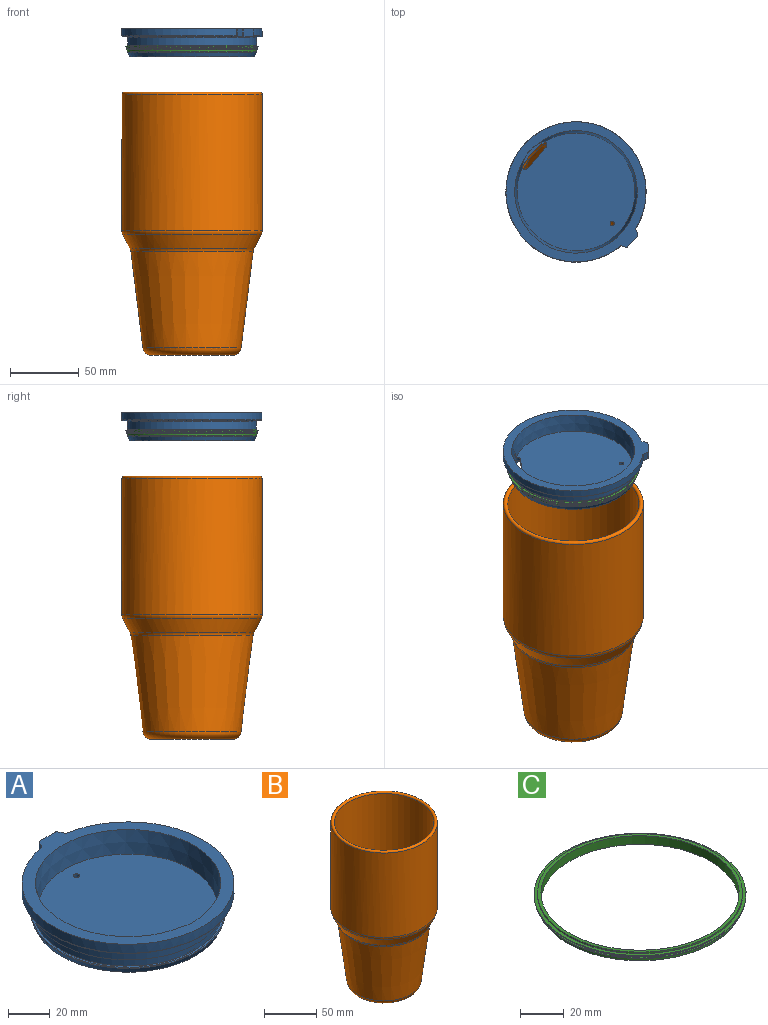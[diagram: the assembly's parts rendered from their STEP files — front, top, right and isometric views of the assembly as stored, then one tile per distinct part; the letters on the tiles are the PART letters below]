
ASSEMBLY  parts=3 mates=5
PART A: 35 faces, bbox 110x110x20.3 mm
  f0: cone r=44.45mm half-angle=7.6deg, axis (0,0,1), area 3346.1mm2, adj f1,f3,f19,f20,f21
  f1: plane 85.41x83.51mm, normal (0,0,1), area 5610.9mm2, adj f0,f16,f17,f18,f19,f20,f23
  f2: plane 85.41x83.51mm, normal (0,0,-1), area 5610.9mm2, adj f15,f16,f17,f18,f19,f20,f23
  f3: plane 105.36x101.6mm, normal (0,0,1), area 1950.2mm2, adj f0,f4,f21,f27,f28,f29,f30,f31
  f4: cylinder r=50.8mm len=101.6mm, axis (0,0,-1), area 1583.8mm2, adj f3,f5,f27,f33
  f5: torus R=50.39mm, axis (0,0,-1), area 200mm2, adj f4,f6,f24,f25,f26,f27,f33
  f6: plane 100.79x100.79mm, normal (0,0,-1), area 870.9mm2, adj f5,f7
  f7: torus R=47.56mm, axis (0,0,-1), area 365.7mm2, adj f6,f8
  f8: cylinder r=46.78mm len=93.55mm, axis (0,0,-1), area 1634.9mm2, adj f7,f9
  f9: plane 93.55x93.55mm, normal (0,0,-1), area 458.7mm2, adj f8,f10
  f10: cylinder r=45.19mm len=90.38mm, axis (0,0,-1), area 1352.2mm2, adj f9,f11
  f11: plane 92.6x92.6mm, normal (0,0,1), area 318.7mm2, adj f10,f12
  f12: torus R=46.3mm, axis (0,0,-1), area 180.7mm2, adj f11,f13
  f13: cone r=46.58mm half-angle=24deg, axis (0,0,1), area 986.6mm2, adj f12,f14
  f14: plane 90.38x90.38mm, normal (0,0,-1), area 686.4mm2, adj f13,f15
  f15: cylinder r=42.7mm len=85.41mm, axis (0,0,-1), area 1241.1mm2, adj f2,f14,f19,f20,f22
  f16: plane 20.19x2.54mm, normal (0,-1,0), area 51.3mm2, adj f1,f2,f17,f18
  f17: cylinder r=3.17mm len=3.14mm, axis (0,0,1), area 11.3mm2, adj f1,f2,f16,f19
  f18: cylinder r=3.17mm len=2.54mm, axis (0,0,1), area 8mm2, adj f1,f2,f16,f20
  f19: cylinder r=1.3mm len=7.04mm, axis (0,0,1), area 6.5mm2, adj f0,f1,f2,f15,f17,f21,f22
  f20: cylinder r=1.3mm len=4.64mm, axis (0,0,1), area 5mm2, adj f0,f1,f2,f15,f18,f21,f22
  f21: cylinder r=22.36mm len=24.5mm, axis (0,0,1), area 357.6mm2, adj f0,f3,f19,f20,f22
  f22: plane 25.42x4.26mm, normal (0,0,1), area 41.9mm2, adj f15,f19,f20,f21
  f23: cylinder r=1.52mm len=3.05mm, axis (0,0,1), area 24.3mm2, adj f1,f2
  f24: plane 0.43x0.22mm, normal (0.16,-0.99,0), area 0.1mm2, adj f5,f25,f33,f34
  f25: cylinder r=50.15mm len=16.4mm, axis (0,0,1), area 3.6mm2, adj f5,f24,f26,f34
  f26: plane 0.43x0.22mm, normal (-0.16,-0.99,0), area 0.1mm2, adj f5,f25,f27,f34
  f27: cylinder r=0.85mm len=5.64mm, axis (0,0,1), area 3.1mm2, adj f3,f4,f5,f26,f28,f34
  f28: plane 5.64x3.39mm, normal (0.89,0.45,0), area 21.4mm2, adj f3,f27,f29,f34
  f29: cylinder r=1.27mm len=5.64mm, axis (0,0,1), area 7.9mm2, adj f3,f28,f30,f34
  f30: plane 10.3x5.64mm, normal (0,1,0), area 58.1mm2, adj f3,f29,f31,f34
  f31: cylinder r=1.27mm len=5.64mm, axis (0,0,1), area 7.9mm2, adj f3,f30,f32,f34
  f32: plane 5.64x3.39mm, normal (-0.89,0.45,0), area 21.4mm2, adj f3,f31,f33,f34
  f33: cylinder r=0.85mm len=5.64mm, axis (0,0,1), area 3.1mm2, adj f3,f4,f5,f24,f32,f34
  f34: plane 17.25x4.54mm, normal (0,0,-1), area 55.7mm2, adj f24,f25,f26,f27,f28,f29,f30,f31
PART B: 14 faces, bbox 110x110x190.6 mm
  f0: plane 55.28x55.28mm, normal (0,0,1), area 2399.7mm2, adj f13
  f1: cone r=41.3mm half-angle=7.1deg, axis (0,0,1), area 16153.7mm2, adj f2,f13
  f2: torus R=44.45mm, axis (0,0,1), area 280.4mm2, adj f1,f3
  f3: cone r=47.62mm half-angle=26.6deg, axis (0,0,1), area 3770.4mm2, adj f2,f4
  f4: cylinder r=47.62mm len=99.37mm, axis (0,0,1), area 29734.9mm2, adj f3,f5
  f5: torus R=49.21mm, axis (0,0,1), area 1542.1mm2, adj f4,f6
  f6: cylinder r=50.8mm len=101.6mm, axis (0,0,1), area 31478mm2, adj f5,f10
  f7: cone r=50.8mm half-angle=26.6deg, axis (0,0,1), area 3468.1mm2, adj f10,f11
  f8: cone r=44.45mm half-angle=7.1deg, axis (0,0,1), area 17603.7mm2, adj f11,f12
  f9: plane 58.64x58.64mm, normal (0,0,-1), area 2700.6mm2, adj f12
  f10: torus R=44.45mm, axis (0,0,-1), area 935.6mm2, adj f6,f7
  f11: torus R=50.62mm, axis (0,0,1), area 603.3mm2, adj f7,f8
  f12: torus R=29.32mm, axis (0,0,-1), area 1914mm2, adj f8,f9
  f13: torus R=27.64mm, axis (0,0,-1), area 1418mm2, adj f0,f1
PART C: 12 faces, bbox 96.7x96.7x4.8 mm
  f0: cylinder r=45.19mm len=90.38mm, axis (0,0,1), area 1352.2mm2, adj f1,f11
  f1: plane 93.55x93.55mm, normal (0,0,-1), area 458.7mm2, adj f0,f2
  f2: cylinder r=46.78mm len=93.55mm, axis (0,0,1), area 463mm2, adj f1,f3
  f3: cone r=47.63mm half-angle=72.7deg, axis (0,0,1), area 266.5mm2, adj f2,f4
  f4: cylinder r=47.63mm len=95.27mm, axis (0,0,1), area 79.8mm2, adj f3,f5
  f5: plane 95.27x95.27mm, normal (0,0,1), area 254.4mm2, adj f4,f6
  f6: cylinder r=46.78mm len=93.55mm, axis (0,0,1), area 313.4mm2, adj f5,f7
  f7: cone r=48.36mm half-angle=73.9deg, axis (0,0,1), area 493.8mm2, adj f6,f8
  f8: cylinder r=48.36mm len=96.73mm, axis (0,0,1), area 102mm2, adj f7,f9
  f9: plane 96.73x96.73mm, normal (0,0,1), area 474.5mm2, adj f8,f10
  f10: cylinder r=46.78mm len=93.55mm, axis (0,0,1), area 233.3mm2, adj f9,f11
  f11: plane 93.55x93.55mm, normal (0,0,1), area 458.7mm2, adj f0,f10
PLACE A rot(axis=(0,0,-1),131.2deg) t=(0,0,97.65)mm
PLACE B at identity fixed
PLACE C rot(axis=(0,0,-1),131.2deg) t=(0,0,85.66)mm
MATE parallel C.f0 <-> A.f0  axis (0,0,1) through (0,0,83.28)mm
MATE parallel A.f0 <-> B.f1  axis (0,0,-1) through (0,0,88.44)mm
MATE cylindrical A.f0 <-> B.f1  axis (0,0,-1) through (0,0,88.44)mm
MATE parallel A.f0 <-> B.f1  axis (0,0,-1) through (0,0,92.01)mm
MATE fastened C.f0 <-> A.f0  axis (0,0,1) through (0,0,83.28)mm
